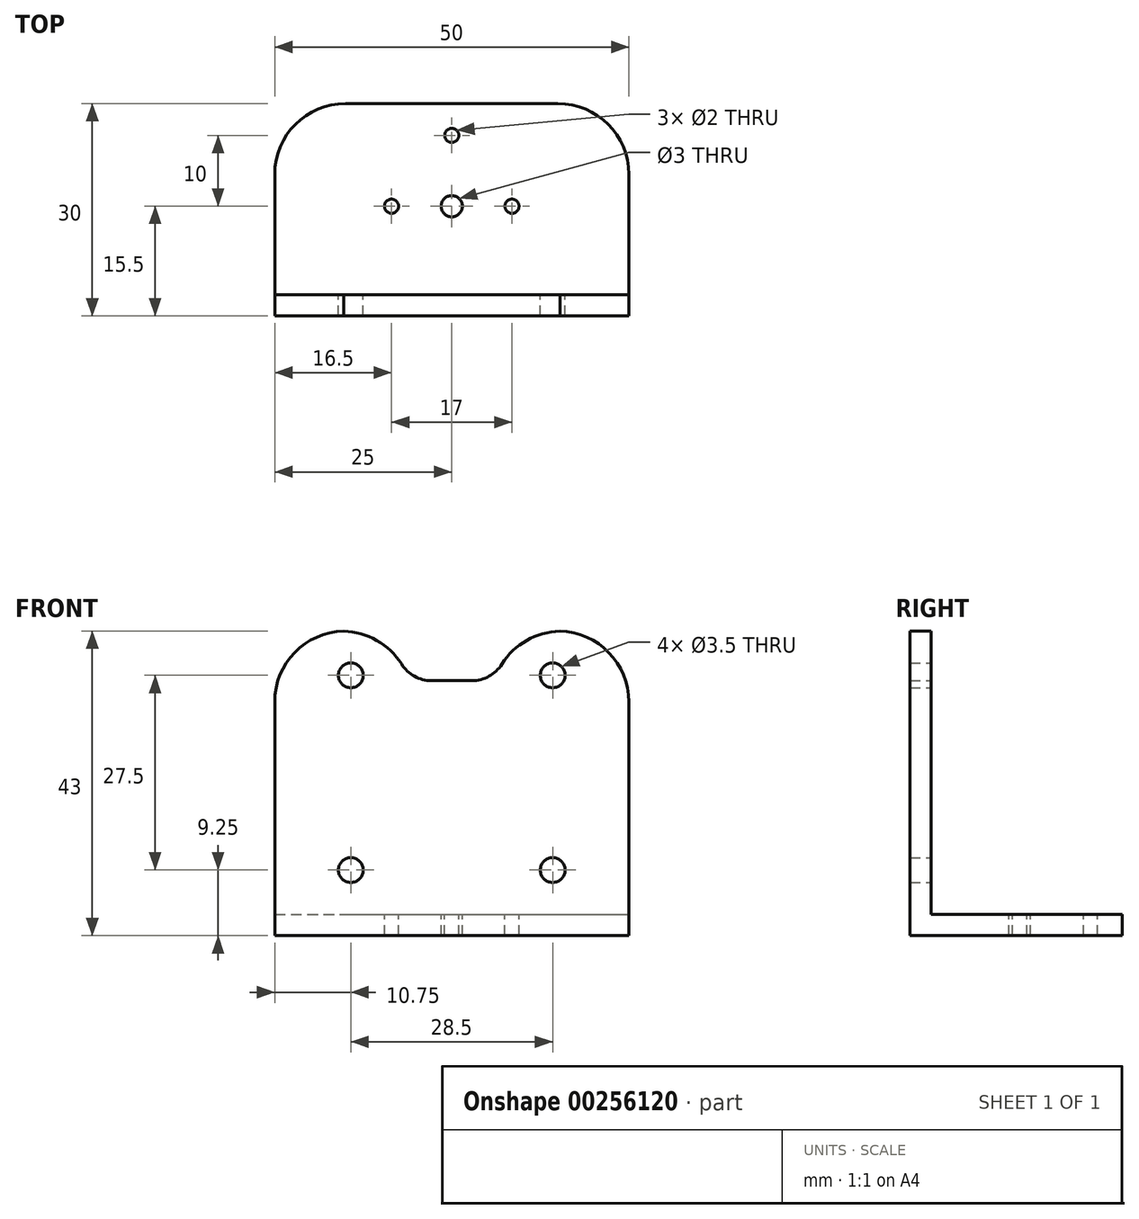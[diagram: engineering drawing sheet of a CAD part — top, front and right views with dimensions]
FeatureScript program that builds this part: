
annotation { "Feature Type Name" : "Feature", "Feature Type Description" : "" }
export const myFeature = defineFeature(function(context is Context, id is Id, definition is map)
    precondition{}
    {
        {
            var Q0;
            Q0=qCreatedBy(makeId("Front.planeOp"),FACE);
            var sketch = newSketch(context, id + "F0", { "sketchPlane" : qUnion([Q0])});
            skLineSegment(sketch, "E0.bottom", {"start": v(-25, 20) * mm, "end": v(25, 20) * mm});
            skLineSegment(sketch, "E0.top", {"start": v(-25, -20) * mm, "end": v(25, -20) * mm});
            skLineSegment(sketch, "E0.left", {"start": v(-25, 20) * mm, "end": v(-25, -20) * mm});
            skLineSegment(sketch, "E0.right", {"start": v(25, 20) * mm, "end": v(25, -20) * mm});
            skPoint(sketch, "E0.middle", {"position": v(0, 0) * mm});
            skCircle(sketch, "E1", {"center": v(-14.25, 13.75) * mm, "radius": 1.75 * mm});
            skCircle(sketch, "E2.MirrorC", {"center": v(14.25, 13.75) * mm, "radius": 1.75 * mm});
            skCircle(sketch, "E3.MirrorC", {"center": v(-14.25, -13.75) * mm, "radius": 1.75 * mm});
            skCircle(sketch, "E4.MirrorC", {"center": v(14.25, -13.75) * mm, "radius": 1.75 * mm});
            skLineSegment(sketch, "E5.bottom", {"start": v(6, 20) * mm, "end": v(-6, 20) * mm});
            skLineSegment(sketch, "E5.top", {"start": v(6, 13) * mm, "end": v(-6, 13) * mm});
            skLineSegment(sketch, "E5.left", {"start": v(6, 20) * mm, "end": v(6, 13) * mm});
            skLineSegment(sketch, "E5.right", {"start": v(-6, 20) * mm, "end": v(-6, 13) * mm});
            skPoint(sketch, "E5.middle", {"position": v(0, 16.5) * mm});
            skSolve(sketch);
        }
        {
            var Q0;
            Q0=makeQuery(id+"F0.imprint","IMPRINT",FACE,{"disambiguationData":[TD([[makeQuery(id+"F0.imprint","IMPRINT",EDGE,{"derivedFrom":sQuery(id+"F0.wireOp",EDGE,"E0.bottom")}),-1.0]])]});
            extrude(context, id + "F1", {"entities" : qUnion([Q0]), "depth" : 3 * mm});
        }
        {
            var Q0;
            Q0=makeQuery(id+"F1.opExtrude","SWEPT_FACE",FACE,{"disambiguationData":[OSD([sQuery(id+"F0.wireOp",EDGE,"E0.top")])]});
            var sketch = newSketch(context, id + "F2", { "sketchPlane" : qUnion([Q0])});
            skLineSegment(sketch, "E6.bottom", {"start": v(-25, 3) * mm, "end": v(25, 3) * mm});
            skLineSegment(sketch, "E6.top", {"start": v(-25, -27) * mm, "end": v(25, -27) * mm});
            skLineSegment(sketch, "E6.left", {"start": v(-25, 3) * mm, "end": v(-25, -27) * mm});
            skLineSegment(sketch, "E6.right", {"start": v(25, 3) * mm, "end": v(25, -27) * mm});
            skCircle(sketch, "E7", {"center": v(0, -12.5) * mm, "radius": 1.5 * mm});
            skCircle(sketch, "E8", {"center": v(-8.5, -12.5) * mm, "radius": 1 * mm});
            skCircle(sketch, "E9.MirrorC", {"center": v(8.5, -12.5) * mm, "radius": 1 * mm});
            skCircle(sketch, "E10", {"center": v(0, -22.5) * mm, "radius": 1 * mm});
            skSolve(sketch);
        }
        {
            var Q0;
            {var subQ0=sQuery(id+"F2.wireOp",EDGE,"E6.bottom");Q0=makeQuery(id+"F2.imprint","IMPRINT",FACE,{"disambiguationData":[TD([[makeQuery(id+"F2.imprint","IMPRINT",EDGE,{"derivedFrom":subQ0}),-1.0]])]});}
            var Q1;
            {var subQ2=sQuery(id+"F2.wireOp",EDGE,"E6.top");Q1=makeQuery(id+"F2.imprint","IMPRINT",FACE,{"disambiguationData":[TD([[makeQuery(id+"F2.imprint","IMPRINT",EDGE,{"derivedFrom":subQ2}),1.0]])]});}
            extrude(context, id + "F3", {"entities" : qUnion([Q0, Q1]), "operationType" : NewBodyOperationType.ADD, "depth" : 3 * mm});
        }
        {
            var Q0;
            Q0=makeQuery(id+"F3.opExtrude","SWEPT_EDGE",EDGE,{"disambiguationData":[OSD([sQuery(id+"F2.wireOp",EDGE,"E6.top"),sQuery(id+"F2.wireOp",EDGE,"E6.right")])]});
            var Q1;
            Q1=makeQuery(id+"F3.opExtrude","SWEPT_EDGE",EDGE,{"disambiguationData":[OSD([sQuery(id+"F2.wireOp",EDGE,"E6.top"),sQuery(id+"F2.wireOp",EDGE,"E6.left")])]});
            var Q2;
            Q2=makeQuery(id+"F1.opExtrude","SWEPT_EDGE",EDGE,{"disambiguationData":[OSD([sQuery(id+"F0.wireOp",EDGE,"E0.bottom"),sQuery(id+"F0.wireOp",EDGE,"E0.left")])]});
            var Q3;
            Q3=makeQuery(id+"F1.opExtrude","SWEPT_EDGE",EDGE,{"disambiguationData":[OSD([sQuery(id+"F0.wireOp",EDGE,"E0.bottom"),sQuery(id+"F0.wireOp",EDGE,"E0.right")])]});
            var Q4;
            Q4=makeQuery(id+"F1.opExtrude","SWEPT_EDGE",EDGE,{"disambiguationData":[OSD([sQuery(id+"F0.wireOp",EDGE,"E0.bottom"),sQuery(id+"F0.wireOp",EDGE,"E5.bottom"),sQuery(id+"F0.wireOp",EDGE,"E5.left")])]});
            var Q5;
            Q5=makeQuery(id+"F1.opExtrude","SWEPT_EDGE",EDGE,{"disambiguationData":[OSD([sQuery(id+"F0.wireOp",EDGE,"E0.bottom"),sQuery(id+"F0.wireOp",EDGE,"E5.bottom"),sQuery(id+"F0.wireOp",EDGE,"E5.right")])]});
            fillet(context, id + "F4", {"entities" : qUnion([Q0, Q1, Q2, Q3, Q4, Q5]), "radius" : 10 * mm, "tangentPropagation" : true, "allowEdgeOverflow" : false});
        }
        {
            var Q0;
            Q0=makeQuery(id+"F4.opFillet","BLEND_EDGE",EDGE,{"blendedFrom":[makeQuery(id+"F1.opExtrude","SWEPT_EDGE",EDGE,{"disambiguationData":[OSD([sQuery(id+"F0.wireOp",EDGE,"E0.bottom"),sQuery(id+"F0.wireOp",EDGE,"E5.bottom"),sQuery(id+"F0.wireOp",EDGE,"E5.left")])]}),makeQuery(id+"F1.opExtrude","SWEPT_FACE",FACE,{"disambiguationData":[OSD([sQuery(id+"F0.wireOp",EDGE,"E5.top")])]})],"blendedInto":[makeQuery(id+"F1.opExtrude","SWEPT_FACE",FACE,{"disambiguationData":[OSD([sQuery(id+"F0.wireOp",EDGE,"E5.top")])]})]});
            var Q1;
            Q1=makeQuery(id+"F4.opFillet","BLEND_EDGE",EDGE,{"blendedFrom":[makeQuery(id+"F1.opExtrude","SWEPT_EDGE",EDGE,{"disambiguationData":[OSD([sQuery(id+"F0.wireOp",EDGE,"E0.bottom"),sQuery(id+"F0.wireOp",EDGE,"E5.bottom"),sQuery(id+"F0.wireOp",EDGE,"E5.right")])]}),makeQuery(id+"F1.opExtrude","SWEPT_FACE",FACE,{"disambiguationData":[OSD([sQuery(id+"F0.wireOp",EDGE,"E5.top")])]})],"blendedInto":[makeQuery(id+"F1.opExtrude","SWEPT_FACE",FACE,{"disambiguationData":[OSD([sQuery(id+"F0.wireOp",EDGE,"E5.top")])]})]});
            fillet(context, id + "F5", {"entities" : qUnion([Q0, Q1]), "radius" : 5 * mm, "tangentPropagation" : true, "allowEdgeOverflow" : false});
        }
    });
